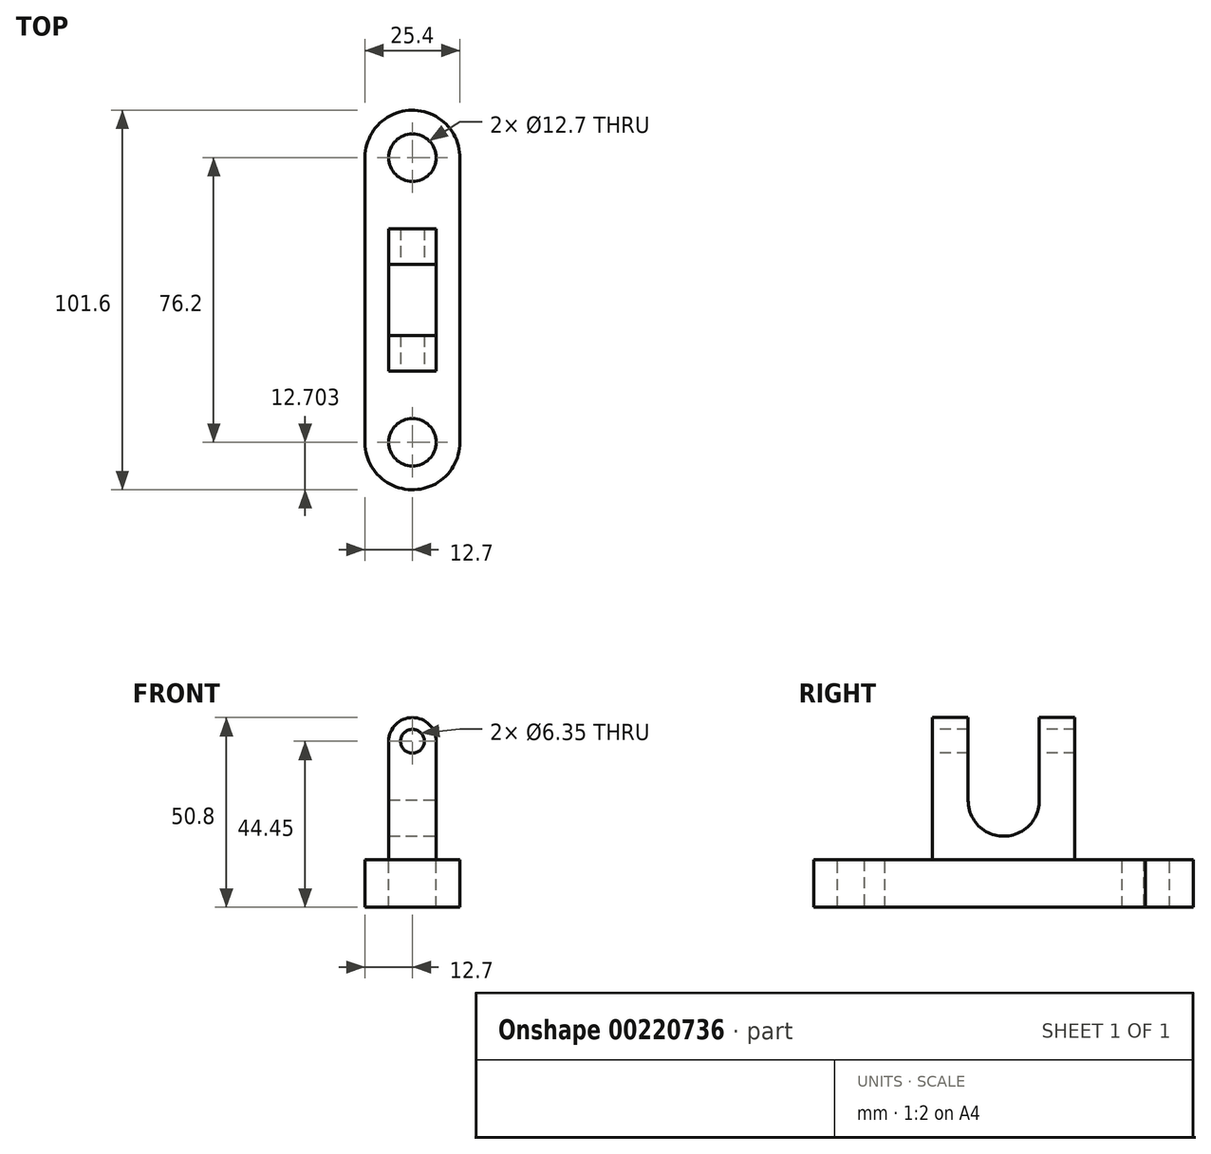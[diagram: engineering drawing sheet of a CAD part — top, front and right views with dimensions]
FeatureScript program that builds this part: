
annotation { "Feature Type Name" : "Feature", "Feature Type Description" : "" }
export const myFeature = defineFeature(function(context is Context, id is Id, definition is map)
    precondition{}
    {
        {
            var Q0;
            Q0=qCreatedBy(makeId("Top.planeOp"),FACE);
            var sketch = newSketch(context, id + "F0", { "sketchPlane" : qUnion([Q0])});
            skArc(sketch, "E0", {"start": v(12.7, 45.1) * mm, "mid": v(-0.23, 58.03) * mm, "end": v(-12.68, 44.64) * mm});
            skArc(sketch, "E1", {"start": v(-12.68, -30.18) * mm, "mid": v(-0.35, -43.56) * mm, "end": v(12.7, -30.87) * mm});
            skLineSegment(sketch, "E2", {"start": v(-12.68, 44.64) * mm, "end": v(-12.68, -31.56) * mm});
            skLineSegment(sketch, "E3", {"start": v(12.7, 45.1) * mm, "end": v(12.7, -30.87) * mm});
            skSolve(sketch);
        }
        {
            var Q0;
            Q0 = qSketchRegion(id + "F0", true);
            extrude(context, id + "F1", {"entities" : qUnion([Q0]), "depth" : 12.7 * mm});
        }
        {
            var Q0;
            Q0=makeQuery(id+"F1.opExtrude","CAP_FACE",FACE,{"disambiguationData":[OSD([sQuery(id+"F0.wireOp",EDGE,"E0"),sQuery(id+"F0.wireOp",EDGE,"E1"),sQuery(id+"F0.wireOp",EDGE,"E2"),sQuery(id+"F0.wireOp",EDGE,"E3")])],"isStart":false});
            var sketch = newSketch(context, id + "F2", { "sketchPlane" : qUnion([Q0])});
            skCircle(sketch, "E4", {"center": v(0, 45.33) * mm, "radius": 6.35 * mm});
            skCircle(sketch, "E5", {"center": v(0, -30.87) * mm, "radius": 6.35 * mm});
            skSolve(sketch);
        }
        {
            var Q0;
            Q0=makeQuery(id+"F2.imprint","IMPRINT",FACE,{"disambiguationData":[TD([[makeQuery(id+"F2.imprint","IMPRINT",EDGE,{"derivedFrom":sQuery(id+"F2.wireOp",EDGE,"E5")}),1.0]])]});
            var Q1;
            Q1=makeQuery(id+"F2.imprint","IMPRINT",FACE,{"disambiguationData":[TD([[makeQuery(id+"F2.imprint","IMPRINT",EDGE,{"derivedFrom":sQuery(id+"F2.wireOp",EDGE,"E4")}),1.0]])]});
            extrude(context, id + "F3", {"entities" : qUnion([Q0, Q1]), "operationType" : NewBodyOperationType.REMOVE, "oppositeDirection" : true, "depth" : 31.24 * mm});
        }
        {
            var Q0;
            Q0=makeQuery(id+"F1.opExtrude","CAP_FACE",FACE,{"disambiguationData":[OSD([sQuery(id+"F0.wireOp",EDGE,"E0"),sQuery(id+"F0.wireOp",EDGE,"E1"),sQuery(id+"F0.wireOp",EDGE,"E2"),sQuery(id+"F0.wireOp",EDGE,"E3")])],"isStart":false});
            var sketch = newSketch(context, id + "F4", { "sketchPlane" : qUnion([Q0])});
            skLineSegment(sketch, "E6", {"start": v(0, 38.98) * mm, "end": v(0, -24.52) * mm});
            skLineSegment(sketch, "E7.bottom", {"start": v(6.35, 26.28) * mm, "end": v(-6.35, 26.28) * mm});
            skLineSegment(sketch, "E7.top", {"start": v(6.35, -11.82) * mm, "end": v(-6.35, -11.82) * mm});
            skLineSegment(sketch, "E7.left", {"start": v(6.35, 26.28) * mm, "end": v(6.35, -11.82) * mm});
            skLineSegment(sketch, "E7.right", {"start": v(-6.35, 26.28) * mm, "end": v(-6.35, -11.82) * mm});
            skPoint(sketch, "E7.middle", {"position": v(0, 7.23) * mm});
            skSolve(sketch);
        }
        {
            var Q0;
            Q0 = qSketchRegion(id + "F4", true);
            extrude(context, id + "F5", {"entities" : qUnion([Q0]), "operationType" : NewBodyOperationType.ADD, "depth" : 38.1 * mm});
        }
        {
            var Q0;
            Q0=makeQuery(id+"F5.opExtrude","SWEPT_FACE",FACE,{"disambiguationData":[OSD([sQuery(id+"F4.wireOp",EDGE,"E7.top")])]});
            var sketch = newSketch(context, id + "F6", { "sketchPlane" : qUnion([Q0])});
            skPoint(sketch, "E8.endSnap0", {"position": v(0, 50.8) * mm});
            skArc(sketch, "E9", {"start": v(6.35, 44.45) * mm, "mid": v(0, 50.8) * mm, "end": v(-6.35, 44.45) * mm});
            skLineSegment(sketch, "E10", {"start": v(-6.35, 44.45) * mm, "end": v(-6.35, 50.8) * mm});
            skLineSegment(sketch, "E11", {"start": v(-6.35, 50.8) * mm, "end": v(6.35, 50.8) * mm});
            skLineSegment(sketch, "E12", {"start": v(6.35, 50.8) * mm, "end": v(6.35, 44.45) * mm});
            skPoint(sketch, "E8.start.orphan", {"position": v(0, 50.8) * mm});
            skSolve(sketch);
        }
        {
            var Q0;
            Q0 = qSketchRegion(id + "F6", true);
            extrude(context, id + "F7", {"entities" : qUnion([Q0]), "operationType" : NewBodyOperationType.REMOVE, "oppositeDirection" : true, "depth" : 61.47 * mm});
        }
        {
            var Q0;
            Q0=makeQuery(id+"F5.opExtrude","SWEPT_FACE",FACE,{"disambiguationData":[OSD([sQuery(id+"F4.wireOp",EDGE,"E7.left")])]});
            var sketch = newSketch(context, id + "F8", { "sketchPlane" : qUnion([Q0])});
            skPoint(sketch, "E13.endSnap0", {"position": v(26.28, 28.58) * mm});
            skArc(sketch, "E14", {"start": v(-2.3, 28.58) * mm, "mid": v(7.32, 19.05) * mm, "end": v(16.76, 28.75) * mm});
            skLineSegment(sketch, "E15", {"start": v(-2.3, 28.58) * mm, "end": v(-2.3, 44.45) * mm});
            skPoint(sketch, "E15.startSnap0", {"position": v(-2.3, 44.45) * mm});
            skLineSegment(sketch, "E16", {"start": v(16.76, 28.75) * mm, "end": v(16.76, 53.78) * mm});
            skLineSegment(sketch, "E17", {"start": v(16.76, 53.78) * mm, "end": v(-2.3, 53.78) * mm});
            skLineSegment(sketch, "E18", {"start": v(-2.3, 53.78) * mm, "end": v(-2.3, 44.45) * mm});
            skPoint(sketch, "E19.orphan", {"position": v(-11.82, 44.45) * mm});
            skPoint(sketch, "E20.orphan", {"position": v(7.23, 44.45) * mm});
            skSolve(sketch);
        }
        {
            var Q0;
            Q0 = qSketchRegion(id + "F8", true);
            extrude(context, id + "F9", {"entities" : qUnion([Q0]), "operationType" : NewBodyOperationType.REMOVE, "oppositeDirection" : true, "depth" : 25.4 * mm});
        }
        {
            var Q0;
            Q0=makeQuery(id+"F5.opExtrude","SWEPT_FACE",FACE,{"disambiguationData":[OSD([sQuery(id+"F4.wireOp",EDGE,"E7.top")])]});
            var sketch = newSketch(context, id + "F10", { "sketchPlane" : qUnion([Q0])});
            skCircle(sketch, "E21", {"center": v(0, 44.45) * mm, "radius": 3.18 * mm});
            skSolve(sketch);
        }
        {
            var Q0;
            Q0 = qSketchRegion(id + "F10", true);
            extrude(context, id + "F11", {"entities" : qUnion([Q0]), "operationType" : NewBodyOperationType.REMOVE, "oppositeDirection" : true, "depth" : 50.8 * mm});
        }
    });
